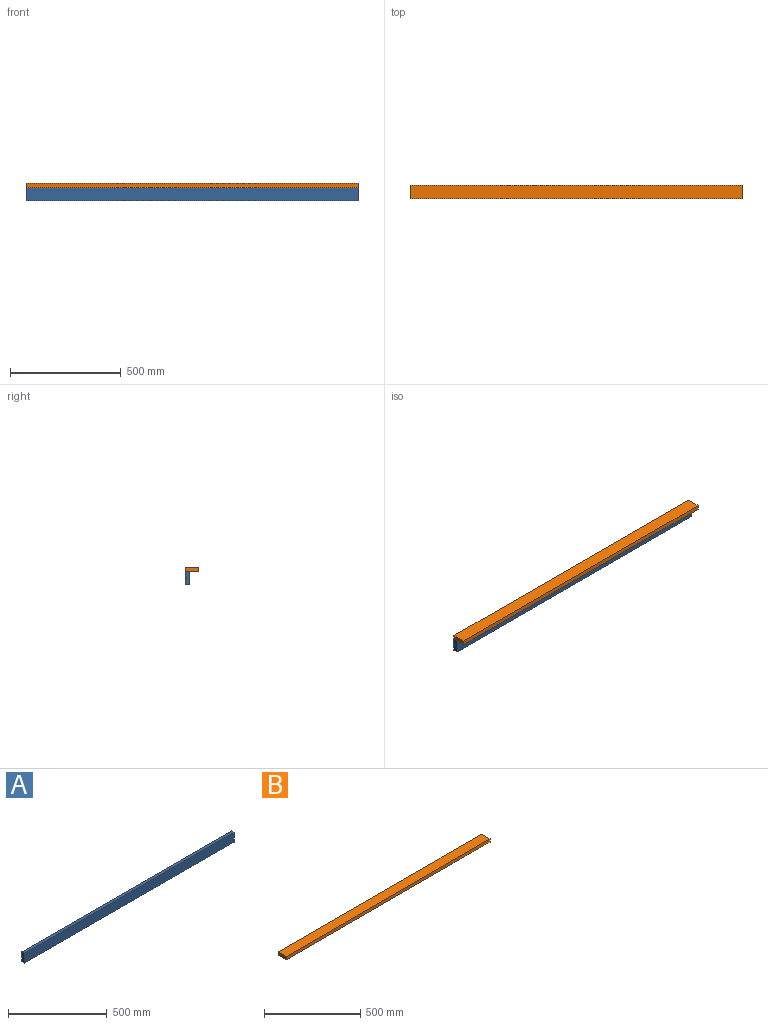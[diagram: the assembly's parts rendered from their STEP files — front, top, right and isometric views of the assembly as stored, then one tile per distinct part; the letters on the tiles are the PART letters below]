
ASSEMBLY  parts=2 mates=1
PART A: 10 faces, bbox 1500x20x60 mm
  f0: plane 1500x29mm, normal (0,1,0), area 43500mm2, adj f1,f3,f4,f9
  f1: plane 60x20mm, normal (1,0,0), area 1170mm2, adj f0,f2,f4,f5,f6,f7,f8,f9
  f2: plane 1500x20mm, normal (0,0,1), area 30000mm2, adj f1,f3,f5,f6
  f3: plane 60x20mm, normal (-1,0,0), area 1170mm2, adj f0,f2,f4,f5,f6,f7,f8,f9
  f4: plane 1500x20mm, normal (0,0,-1), area 30000mm2, adj f0,f1,f3,f6
  f5: plane 1500x25mm, normal (0,1,0), area 37500mm2, adj f1,f2,f3,f7
  f6: plane 1500x60mm, normal (0,-1,0), area 90000mm2, adj f1,f2,f3,f4
  f7: plane 1500x5mm, normal (0,0,-1), area 7500mm2, adj f1,f3,f5,f8
  f8: plane 1500x6mm, normal (0,1,0), area 9000mm2, adj f1,f3,f7,f9
  f9: plane 1500x5mm, normal (0,0,1), area 7500mm2, adj f0,f1,f3,f8
PART B: 6 faces, bbox 1500x60x20 mm
  f0: plane 60x20mm, normal (-1,0,0), area 1200mm2, adj f1,f3,f4,f5
  f1: plane 1500x20mm, normal (0,-1,0), area 30000mm2, adj f0,f2,f4,f5
  f2: plane 60x20mm, normal (1,0,0), area 1200mm2, adj f1,f3,f4,f5
  f3: plane 1500x20mm, normal (0,1,0), area 30000mm2, adj f0,f2,f4,f5
  f4: plane 1500x60mm, normal (0,0,1), area 90000mm2, adj f0,f1,f2,f3
  f5: plane 1500x60mm, normal (0,0,-1), area 90000mm2, adj f0,f1,f2,f3
PLACE A t=(0,40,-60)mm
PLACE B at identity
MATE fastened A.f3 <-> B.f0  axis (-1,0,0) through (0,60,0)mm
